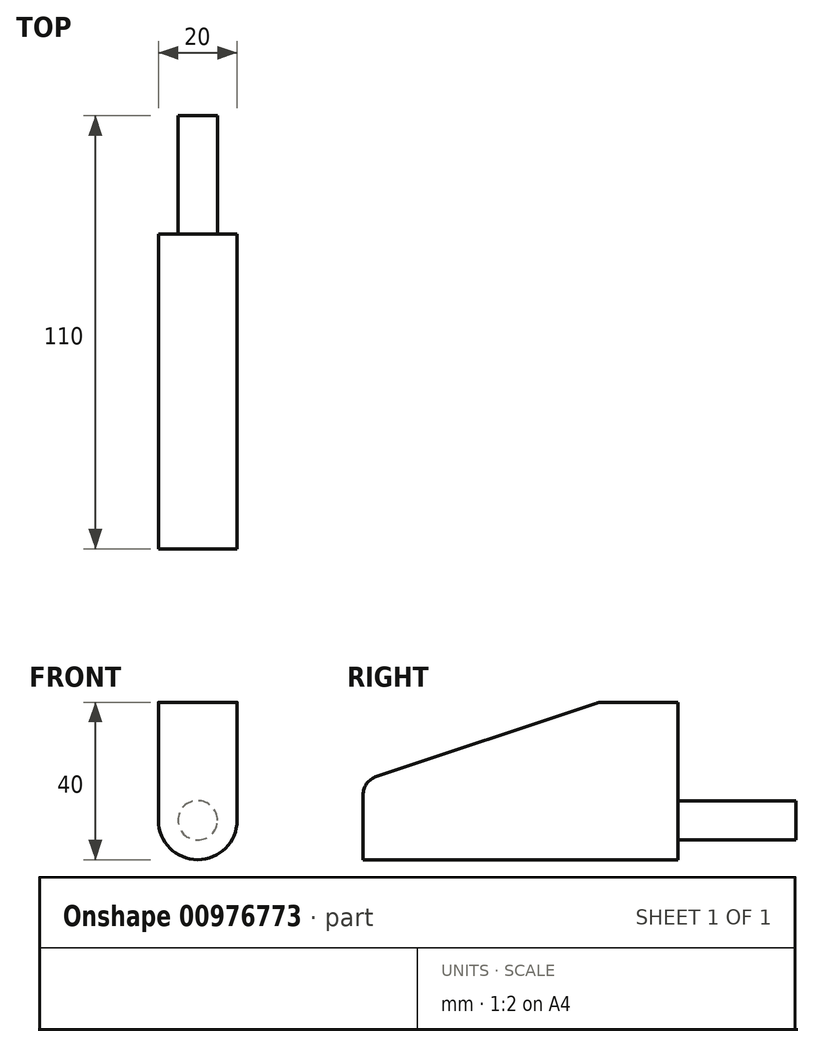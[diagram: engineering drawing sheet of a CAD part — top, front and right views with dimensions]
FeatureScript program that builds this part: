
annotation { "Feature Type Name" : "Feature", "Feature Type Description" : "" }
export const myFeature = defineFeature(function(context is Context, id is Id, definition is map)
    precondition{}
    {
        {
            var Q0;
            Q0=qCreatedBy(makeId("Right.planeOp"),FACE);
            var sketch = newSketch(context, id + "F0", { "sketchPlane" : qUnion([Q0])});
            skLineSegment(sketch, "E0", {"start": v(0, 0) * mm, "end": v(-80, 0) * mm});
            skLineSegment(sketch, "E1", {"start": v(-80, 0) * mm, "end": v(-80, 16.4) * mm});
            skLineSegment(sketch, "E2", {"start": v(-76.58, 21.14) * mm, "end": v(-20.77, 39.74) * mm});
            skLineSegment(sketch, "E3", {"start": v(-19.19, 40) * mm, "end": v(0, 40) * mm});
            skLineSegment(sketch, "E4", {"start": v(0, 40) * mm, "end": v(0, 0) * mm});
            skPoint(sketch, "E5.visualSharp", {"position": v(-80, 20) * mm});
            skArc(sketch, "E5.filletArc", {"start": v(-76.58, 21.14) * mm, "mid": v(-79.06, 19.32) * mm, "end": v(-80, 16.4) * mm});
            skPoint(sketch, "E6.visualSharp", {"position": v(-20, 40) * mm});
            skArc(sketch, "E6.filletArc", {"start": v(-19.19, 40) * mm, "mid": v(-19.99, 39.94) * mm, "end": v(-20.77, 39.74) * mm});
            skSolve(sketch);
        }
        {
            var Q0;
            Q0 = qSketchRegion(id + "F0", true);
            extrude(context, id + "F1", {"entities" : qUnion([Q0]), "depth" : 20 * mm, "offsetDistance" : 25 * mm});
        }
        {
            var Q0;
            Q0=makeQuery(id+"F1.opExtrude","CAP_EDGE",EDGE,{"disambiguationData":[OSD([sQuery(id+"F0.wireOp",EDGE,"E0")])],"isStart":false});
            var Q1;
            Q1=makeQuery(id+"F1.opExtrude","CAP_EDGE",EDGE,{"disambiguationData":[OSD([sQuery(id+"F0.wireOp",EDGE,"E0")])],"isStart":true});
            fillet(context, id + "F2", {"entities" : qUnion([Q0, Q1]), "radius" : 10 * mm, "tangentPropagation" : true, "allowEdgeOverflow" : false});
        }
        {
            var Q0;
            Q0=makeQuery(id+"F1.opExtrude","SWEPT_FACE",FACE,{"disambiguationData":[OSD([sQuery(id+"F0.wireOp",EDGE,"E4")])]});
            var sketch = newSketch(context, id + "F3", { "sketchPlane" : qUnion([Q0])});
            skCircle(sketch, "E7", {"center": v(-10, 10) * mm, "radius": 5 * mm});
            skSolve(sketch);
        }
        {
            var Q0;
            Q0 = qSketchRegion(id + "F3", true);
            extrude(context, id + "F4", {"entities" : qUnion([Q0]), "operationType" : NewBodyOperationType.ADD, "depth" : 30 * mm, "offsetDistance" : 25 * mm});
        }
    });
